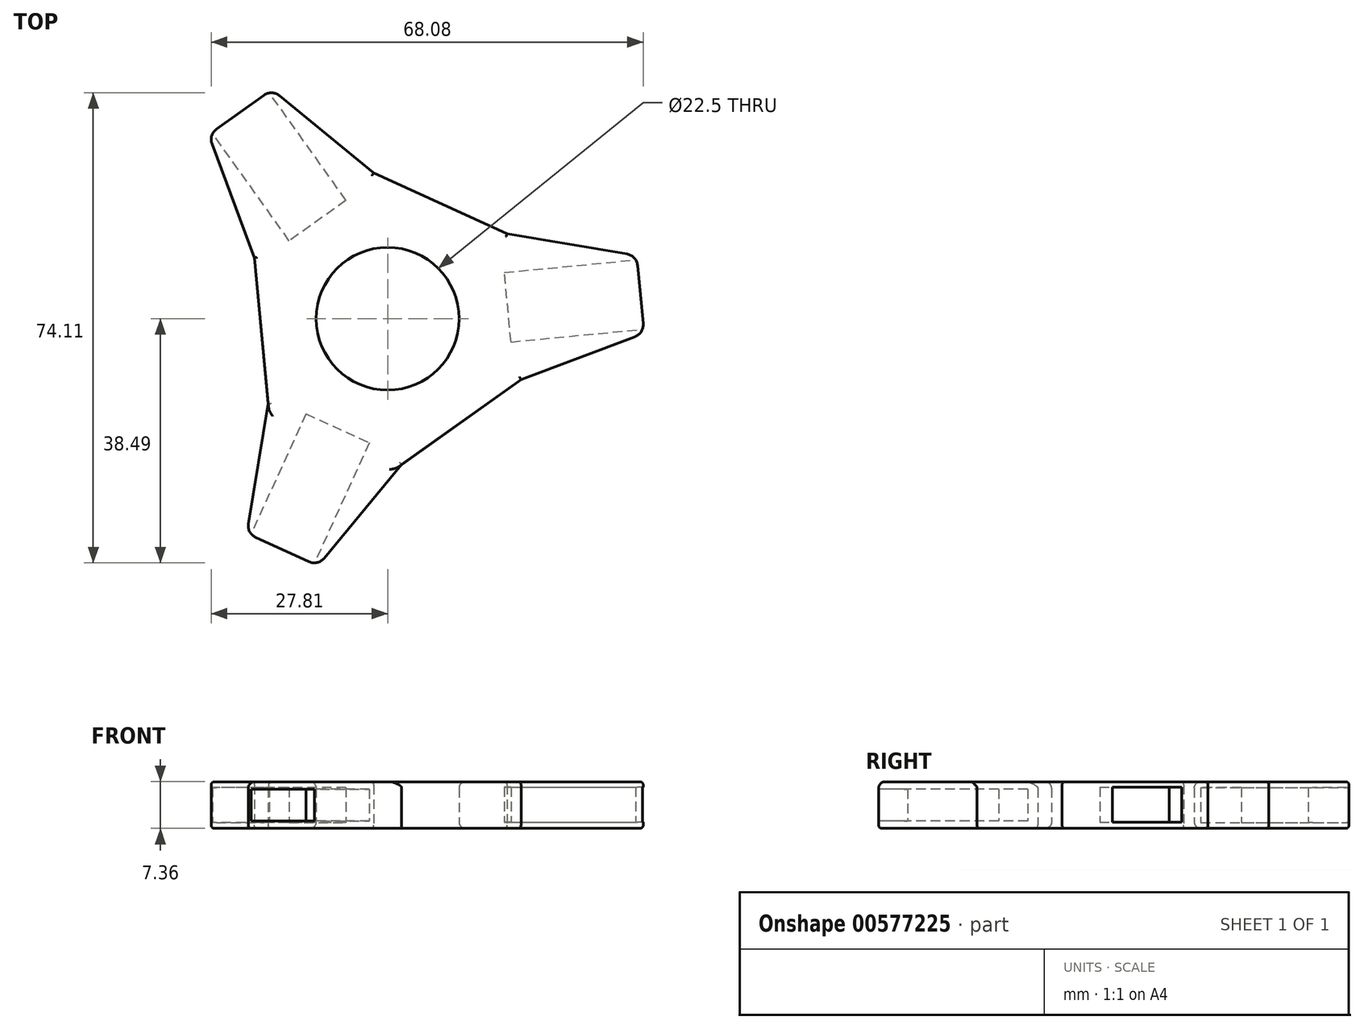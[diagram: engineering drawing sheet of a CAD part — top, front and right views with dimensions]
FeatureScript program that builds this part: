
annotation { "Feature Type Name" : "Feature", "Feature Type Description" : "" }
export const myFeature = defineFeature(function(context is Context, id is Id, definition is map)
    precondition{}
    {
        {
            var Q0;
            Q0=qCreatedBy(makeId("Top.planeOp"),FACE);
            var sketch = newSketch(context, id + "F0", { "sketchPlane" : qUnion([Q0])});
            skCircle(sketch, "E0", {"center": v(0, 0) * mm, "radius": 11.25 * mm});
            skPoint(sketch, "E1.0.midPoint", {"position": v(19.9, 1.91) * mm});
            skLineSegment(sketch, "E2", {"start": v(-21.01, 9.58) * mm, "end": v(-28.22, 29) * mm});
            skLineSegment(sketch, "E3", {"start": v(-28.22, 29) * mm, "end": v(-18.22, 36.13) * mm});
            skLineSegment(sketch, "E4", {"start": v(-18.22, 36.13) * mm, "end": v(-2.2, 22.99) * mm});
            skPoint(sketch, "E5.center", {"position": v(0, 0.71) * mm});
            skLineSegment(sketch, "E6.1.0", {"start": v(2.2, -22.99) * mm, "end": v(-11, -38.94) * mm});
            skLineSegment(sketch, "E6.1.4", {"start": v(-22.18, -33.85) * mm, "end": v(-18.8, -13.4) * mm});
            skLineSegment(sketch, "E6.1.5", {"start": v(-11, -38.94) * mm, "end": v(-22.18, -33.85) * mm});
            skLineSegment(sketch, "E6.2.0", {"start": v(18.8, 13.4) * mm, "end": v(39.23, 9.94) * mm});
            skLineSegment(sketch, "E6.2.4", {"start": v(40.4, -2.29) * mm, "end": v(21.01, -9.58) * mm});
            skLineSegment(sketch, "E6.2.5", {"start": v(39.23, 9.94) * mm, "end": v(40.4, -2.29) * mm});
            skCircle(sketch, "E7.cCircle", {"center": v(0, 0) * mm, "radius": 20 * mm, "construction": true});
            skLineSegment(sketch, "E7.0", {"start": v(18.8, 13.4) * mm, "end": v(21.01, -9.58) * mm});
            skLineSegment(sketch, "E7.2", {"start": v(2.2, -22.99) * mm, "end": v(-18.8, -13.4) * mm});
            skLineSegment(sketch, "E7.3", {"start": v(-18.8, -13.4) * mm, "end": v(-21.01, 9.58) * mm});
            skLineSegment(sketch, "E7.4", {"start": v(-21.01, 9.58) * mm, "end": v(-2.2, 22.99) * mm});
            skLineSegment(sketch, "E7.5", {"start": v(-2.2, 22.99) * mm, "end": v(18.8, 13.4) * mm});
            skLineSegment(sketch, "E8", {"start": v(2.2, -22.99) * mm, "end": v(21.01, -9.58) * mm});
            skSolve(sketch);
        }
        {
            var Q0;
            Q0 = qSketchRegion(id + "F0", true);
            extrude(context, id + "F1", {"entities" : qUnion([Q0]), "endBound" : BoundingType.SYMMETRIC, "depth" : 4.35 * mm, "offsetDistance" : 25 * mm});
        }
        {
            var Q0;
            Q0=makeQuery(id+"F1.opExtrude","CAP_FACE",FACE,{"disambiguationData":[OSD([sQuery(id+"F0.wireOp",EDGE,"E0"),sQuery(id+"F0.wireOp",EDGE,"E1.1"),sQuery(id+"F0.wireOp",EDGE,"E1.3"),sQuery(id+"F0.wireOp",EDGE,"E1.5"),sQuery(id+"F0.wireOp",EDGE,"E2"),sQuery(id+"F0.wireOp",EDGE,"E3"),sQuery(id+"F0.wireOp",EDGE,"E4"),sQuery(id+"F0.wireOp",EDGE,"IyGyZZ2j-7i47-TdS6-ERBN-ua2aBuEQpkr1.bottom"),sQuery(id+"F0.wireOp",EDGE,"IyGyZZ2j-7i47-TdS6-ERBN-ua2aBuEQpkr1.top"),sQuery(id+"F0.wireOp",EDGE,"IyGyZZ2j-7i47-TdS6-ERBN-ua2aBuEQpkr1.left"),sQuery(id+"F0.wireOp",EDGE,"IyGyZZ2j-7i47-TdS6-ERBN-ua2aBuEQpkr1.right"),sQuery(id+"F0.wireOp",EDGE,"MXUuy9MU-6Gwn-W3UW-Jdoq-sXBRnCOHbCZX.bottom"),sQuery(id+"F0.wireOp",EDGE,"MXUuy9MU-6Gwn-W3UW-Jdoq-sXBRnCOHbCZX.top"),sQuery(id+"F0.wireOp",EDGE,"MXUuy9MU-6Gwn-W3UW-Jdoq-sXBRnCOHbCZX.left"),sQuery(id+"F0.wireOp",EDGE,"MXUuy9MU-6Gwn-W3UW-Jdoq-sXBRnCOHbCZX.right"),sQuery(id+"F0.wireOp",EDGE,"6431977e-7dac-4d3b-9058-e1544c9c4d50.1.0"),sQuery(id+"F0.wireOp",EDGE,"6431977e-7dac-4d3b-9058-e1544c9c4d50.1.1"),sQuery(id+"F0.wireOp",EDGE,"6431977e-7dac-4d3b-9058-e1544c9c4d50.1.2"),sQuery(id+"F0.wireOp",EDGE,"6431977e-7dac-4d3b-9058-e1544c9c4d50.1.3"),sQuery(id+"F0.wireOp",EDGE,"6431977e-7dac-4d3b-9058-e1544c9c4d50.1.4"),sQuery(id+"F0.wireOp",EDGE,"6431977e-7dac-4d3b-9058-e1544c9c4d50.1.5"),sQuery(id+"F0.wireOp",EDGE,"6431977e-7dac-4d3b-9058-e1544c9c4d50.1.6"),sQuery(id+"F0.wireOp",EDGE,"6431977e-7dac-4d3b-9058-e1544c9c4d50.1.7"),sQuery(id+"F0.wireOp",EDGE,"6431977e-7dac-4d3b-9058-e1544c9c4d50.1.8"),sQuery(id+"F0.wireOp",EDGE,"6431977e-7dac-4d3b-9058-e1544c9c4d50.1.9"),sQuery(id+"F0.wireOp",EDGE,"6431977e-7dac-4d3b-9058-e1544c9c4d50.1.10"),sQuery(id+"F0.wireOp",EDGE,"6431977e-7dac-4d3b-9058-e1544c9c4d50.2.0"),sQuery(id+"F0.wireOp",EDGE,"6431977e-7dac-4d3b-9058-e1544c9c4d50.2.1"),sQuery(id+"F0.wireOp",EDGE,"6431977e-7dac-4d3b-9058-e1544c9c4d50.2.2"),sQuery(id+"F0.wireOp",EDGE,"6431977e-7dac-4d3b-9058-e1544c9c4d50.2.3"),sQuery(id+"F0.wireOp",EDGE,"6431977e-7dac-4d3b-9058-e1544c9c4d50.2.4"),sQuery(id+"F0.wireOp",EDGE,"6431977e-7dac-4d3b-9058-e1544c9c4d50.2.5"),sQuery(id+"F0.wireOp",EDGE,"6431977e-7dac-4d3b-9058-e1544c9c4d50.2.6"),sQuery(id+"F0.wireOp",EDGE,"6431977e-7dac-4d3b-9058-e1544c9c4d50.2.7"),sQuery(id+"F0.wireOp",EDGE,"6431977e-7dac-4d3b-9058-e1544c9c4d50.2.8"),sQuery(id+"F0.wireOp",EDGE,"6431977e-7dac-4d3b-9058-e1544c9c4d50.2.9"),sQuery(id+"F0.wireOp",EDGE,"6431977e-7dac-4d3b-9058-e1544c9c4d50.2.10")])],"isStart":false});
            var sketch = newSketch(context, id + "F2", { "sketchPlane" : qUnion([Q0])});
            skLineSegment(sketch, "E9", {"start": v(-22.18, -33.85) * mm, "end": v(-18.8, -13.4) * mm});
            skLineSegment(sketch, "E10", {"start": v(-28.22, 29) * mm, "end": v(-28.22, 29) * mm});
            skLineSegment(sketch, "E11", {"start": v(-28.22, 29) * mm, "end": v(-18.22, 36.13) * mm});
            skLineSegment(sketch, "E12", {"start": v(-18.22, 36.13) * mm, "end": v(-18.22, 36.13) * mm});
            skLineSegment(sketch, "E13", {"start": v(39.23, 9.94) * mm, "end": v(40.4, -2.29) * mm});
            skLineSegment(sketch, "E14", {"start": v(-11, -38.94) * mm, "end": v(-22.18, -33.85) * mm});
            skCircle(sketch, "E15", {"center": v(0, 0) * mm, "radius": 11.25 * mm});
            skLineSegment(sketch, "E16", {"start": v(39.23, 9.94) * mm, "end": v(39.23, 9.94) * mm});
            skLineSegment(sketch, "E17", {"start": v(40.4, -2.29) * mm, "end": v(40.4, -2.29) * mm});
            skLineSegment(sketch, "E18", {"start": v(-11, -38.94) * mm, "end": v(-11, -38.94) * mm});
            skLineSegment(sketch, "E19", {"start": v(-18.8, -13.4) * mm, "end": v(-21.01, 9.58) * mm});
            skLineSegment(sketch, "E20", {"start": v(-21.01, 9.58) * mm, "end": v(-28.22, 29) * mm});
            skLineSegment(sketch, "E21", {"start": v(-18.22, 36.13) * mm, "end": v(-2.2, 22.99) * mm});
            skLineSegment(sketch, "E22", {"start": v(-2.2, 22.99) * mm, "end": v(18.8, 13.4) * mm});
            skLineSegment(sketch, "E23", {"start": v(18.8, 13.4) * mm, "end": v(39.23, 9.94) * mm});
            skLineSegment(sketch, "E24", {"start": v(40.4, -2.29) * mm, "end": v(21.01, -9.58) * mm});
            skLineSegment(sketch, "E25", {"start": v(21.01, -9.58) * mm, "end": v(2.2, -22.99) * mm});
            skLineSegment(sketch, "E26", {"start": v(2.2, -22.99) * mm, "end": v(-11, -38.94) * mm});
            skSolve(sketch);
        }
        {
            var Q0;
            Q0 = qSketchRegion(id + "F2", true);
            extrude(context, id + "F3", {"entities" : qUnion([Q0]), "operationType" : NewBodyOperationType.ADD, "depth" : 1.5 * mm, "offsetDistance" : 25 * mm});
        }
        {
            var Q0;
            Q0=makeQuery(id+"F1.opExtrude","SWEPT_BODY",BODY,{"disambiguationData":[OSD([sQuery(id+"F0.wireOp",EDGE,"E0"),sQuery(id+"F0.wireOp",EDGE,"E1.1"),sQuery(id+"F0.wireOp",EDGE,"E1.3"),sQuery(id+"F0.wireOp",EDGE,"E1.5"),sQuery(id+"F0.wireOp",EDGE,"E2"),sQuery(id+"F0.wireOp",EDGE,"E3"),sQuery(id+"F0.wireOp",EDGE,"E4"),sQuery(id+"F0.wireOp",EDGE,"EbaCOkDP-zAhZ-bmKm-Rwlq-MVlfTA77LE2a"),sQuery(id+"F0.wireOp",EDGE,"XpNV4llA-Ck6J-PTxp-DKK9-vu7mp3MRyvdA"),sQuery(id+"F0.wireOp",EDGE,"A7reB7LC-x8tl-05Yz-VyCx-lSxhYCwyqfyA"),sQuery(id+"F0.wireOp",EDGE,"CRzMPJHI-l73M-eAgr-tN1m-DsJvh2o7b73Q"),sQuery(id+"F0.wireOp",EDGE,"E6.1.0"),sQuery(id+"F0.wireOp",EDGE,"E6.1.1"),sQuery(id+"F0.wireOp",EDGE,"E6.1.2"),sQuery(id+"F0.wireOp",EDGE,"E6.1.3"),sQuery(id+"F0.wireOp",EDGE,"E6.1.4"),sQuery(id+"F0.wireOp",EDGE,"E6.1.5"),sQuery(id+"F0.wireOp",EDGE,"E6.1.6"),sQuery(id+"F0.wireOp",EDGE,"E6.2.0"),sQuery(id+"F0.wireOp",EDGE,"E6.2.1"),sQuery(id+"F0.wireOp",EDGE,"E6.2.2"),sQuery(id+"F0.wireOp",EDGE,"E6.2.3"),sQuery(id+"F0.wireOp",EDGE,"E6.2.4"),sQuery(id+"F0.wireOp",EDGE,"E6.2.5"),sQuery(id+"F0.wireOp",EDGE,"E6.2.6")])]});
            var Q1;
            Q1=qCreatedBy(makeId("Top.planeOp"),FACE);
            mirror(context, id + "F4", {"operationType" : NewBodyOperationType.ADD, "entities" : qUnion([Q0]), "mirrorPlane" : qUnion([Q1])});
        }
        {
            var Q0;
            {var subQ0=makeQuery(id+"F3.boolean.opBoolean","MERGE",FACE,{"derivedFrom":[makeQuery(id+"F1.opExtrude","SWEPT_FACE",FACE,{"disambiguationData":[OSD([sQuery(id+"F0.wireOp",EDGE,"E6.2.5")])]}),makeQuery(id+"F3.opExtrude","SWEPT_FACE",FACE,{"disambiguationData":[OSD([sQuery(id+"F2.wireOp",EDGE,"E13")])]})]});Q0=makeQuery(id+"F4.boolean.opBoolean","MERGE",FACE,{"derivedFrom":[subQ0,makeQuery(id+"F4.opPattern","COPY",FACE,{"derivedFrom":subQ0,"instanceName":"1"})]});}
            var sketch = newSketch(context, id + "F5", { "sketchPlane" : qUnion([Q0])});
            skLineSegment(sketch, "E27.bottom", {"start": v(-5.5, 2.82) * mm, "end": v(5.5, 2.82) * mm});
            skLineSegment(sketch, "E27.top", {"start": v(-5.5, -2.67) * mm, "end": v(5.5, -2.67) * mm});
            skLineSegment(sketch, "E27.left", {"start": v(-5.5, 2.82) * mm, "end": v(-5.5, -2.67) * mm});
            skLineSegment(sketch, "E27.right", {"start": v(5.5, 2.82) * mm, "end": v(5.5, -2.67) * mm});
            skSolve(sketch);
        }
        {
            var Q0;
            Q0 = qSketchRegion(id + "F5", true);
            extrude(context, id + "F6", {"entities" : qUnion([Q0]), "operationType" : NewBodyOperationType.REMOVE, "oppositeDirection" : true, "depth" : 21 * mm, "offsetDistance" : 25 * mm});
        }
        {
            var Q0;
            {var subQ0=makeQuery(id+"F3.boolean.opBoolean","MERGE",FACE,{"derivedFrom":[makeQuery(id+"F1.opExtrude","SWEPT_FACE",FACE,{"disambiguationData":[OSD([sQuery(id+"F0.wireOp",EDGE,"E3")])]}),makeQuery(id+"F3.opExtrude","SWEPT_FACE",FACE,{"disambiguationData":[OSD([sQuery(id+"F2.wireOp",EDGE,"E11")])]})]});Q0=makeQuery(id+"F4.boolean.opBoolean","MERGE",FACE,{"derivedFrom":[subQ0,makeQuery(id+"F4.opPattern","COPY",FACE,{"derivedFrom":subQ0,"instanceName":"1"})]});}
            var sketch = newSketch(context, id + "F7", { "sketchPlane" : qUnion([Q0])});
            skLineSegment(sketch, "E28.left", {"start": v(-5.5, 2.75) * mm, "end": v(-5.5, -2.75) * mm});
            skLineSegment(sketch, "E29", {"start": v(-5.5, 2.75) * mm, "end": v(5.5, 2.75) * mm});
            skLineSegment(sketch, "E30", {"start": v(5.5, 2.75) * mm, "end": v(5.5, -2.75) * mm});
            skLineSegment(sketch, "E31", {"start": v(5.5, -2.75) * mm, "end": v(-5.5, -2.75) * mm});
            skSolve(sketch);
        }
        {
            var Q0;
            Q0 = qSketchRegion(id + "F7", true);
            extrude(context, id + "F8", {"entities" : qUnion([Q0]), "operationType" : NewBodyOperationType.REMOVE, "oppositeDirection" : true, "depth" : 21 * mm, "offsetDistance" : 25 * mm});
        }
        {
            var Q0;
            {var subQ0=makeQuery(id+"F3.boolean.opBoolean","MERGE",FACE,{"derivedFrom":[makeQuery(id+"F1.opExtrude","SWEPT_FACE",FACE,{"disambiguationData":[OSD([sQuery(id+"F0.wireOp",EDGE,"E6.1.5")])]}),makeQuery(id+"F3.opExtrude","SWEPT_FACE",FACE,{"disambiguationData":[OSD([sQuery(id+"F2.wireOp",EDGE,"E14")])]})]});Q0=makeQuery(id+"F4.boolean.opBoolean","MERGE",FACE,{"derivedFrom":[subQ0,makeQuery(id+"F4.opPattern","COPY",FACE,{"derivedFrom":subQ0,"instanceName":"1"})]});}
            var sketch = newSketch(context, id + "F9", { "sketchPlane" : qUnion([Q0])});
            skLineSegment(sketch, "E32.bottom", {"start": v(-5.5, 2.5) * mm, "end": v(5.5, 2.5) * mm});
            skLineSegment(sketch, "E32.top", {"start": v(-5.5, -2.5) * mm, "end": v(5.5, -2.5) * mm});
            skLineSegment(sketch, "E32.left", {"start": v(-5.5, 2.5) * mm, "end": v(-5.5, -2.5) * mm});
            skLineSegment(sketch, "E32.right", {"start": v(5.5, 2.5) * mm, "end": v(5.5, -2.5) * mm});
            skSolve(sketch);
        }
        {
            var Q0;
            Q0 = qSketchRegion(id + "F9", true);
            extrude(context, id + "F10", {"entities" : qUnion([Q0]), "operationType" : NewBodyOperationType.REMOVE, "oppositeDirection" : true, "depth" : 21 * mm, "offsetDistance" : 25 * mm});
        }
        {
            var Q0;
            {var subQ0=makeQuery(id+"F3.boolean.opBoolean","MERGE",EDGE,{"derivedFrom":[makeQuery(id+"F1.opExtrude","SWEPT_EDGE",EDGE,{"disambiguationData":[OSD([sQuery(id+"F0.wireOp",EDGE,"E3"),sQuery(id+"F0.wireOp",EDGE,"E4")])]}),makeQuery(id+"F3.opExtrude","SWEPT_EDGE",EDGE,{"disambiguationData":[OSD([sQuery(id+"F2.wireOp",EDGE,"E11"),sQuery(id+"F2.wireOp",EDGE,"E21")])]})]});Q0=makeQuery(id+"F4.boolean.opBoolean","MERGE",EDGE,{"derivedFrom":[subQ0,makeQuery(id+"F4.opPattern","COPY",EDGE,{"derivedFrom":subQ0,"instanceName":"1"})]});}
            var Q1;
            {var subQ0=makeQuery(id+"F3.boolean.opBoolean","MERGE",EDGE,{"derivedFrom":[makeQuery(id+"F1.opExtrude","SWEPT_EDGE",EDGE,{"disambiguationData":[OSD([sQuery(id+"F0.wireOp",EDGE,"E2"),sQuery(id+"F0.wireOp",EDGE,"E3")])]}),makeQuery(id+"F3.opExtrude","SWEPT_EDGE",EDGE,{"disambiguationData":[OSD([sQuery(id+"F2.wireOp",EDGE,"E11"),sQuery(id+"F2.wireOp",EDGE,"E20")])]})]});Q1=makeQuery(id+"F4.boolean.opBoolean","MERGE",EDGE,{"derivedFrom":[subQ0,makeQuery(id+"F4.opPattern","COPY",EDGE,{"derivedFrom":subQ0,"instanceName":"1"})]});}
            var Q2;
            {var subQ0=makeQuery(id+"F3.boolean.opBoolean","MERGE",EDGE,{"derivedFrom":[makeQuery(id+"F1.opExtrude","SWEPT_EDGE",EDGE,{"disambiguationData":[OSD([sQuery(id+"F0.wireOp",EDGE,"E6.1.4"),sQuery(id+"F0.wireOp",EDGE,"E6.1.5")])]}),makeQuery(id+"F3.opExtrude","SWEPT_EDGE",EDGE,{"disambiguationData":[OSD([sQuery(id+"F2.wireOp",EDGE,"E9"),sQuery(id+"F2.wireOp",EDGE,"E14")])]})]});Q2=makeQuery(id+"F4.boolean.opBoolean","MERGE",EDGE,{"derivedFrom":[subQ0,makeQuery(id+"F4.opPattern","COPY",EDGE,{"derivedFrom":subQ0,"instanceName":"1"})]});}
            var Q3;
            {var subQ0=makeQuery(id+"F3.boolean.opBoolean","MERGE",EDGE,{"derivedFrom":[makeQuery(id+"F1.opExtrude","SWEPT_EDGE",EDGE,{"disambiguationData":[OSD([sQuery(id+"F0.wireOp",EDGE,"E6.1.0"),sQuery(id+"F0.wireOp",EDGE,"E6.1.5")])]}),makeQuery(id+"F3.opExtrude","SWEPT_EDGE",EDGE,{"disambiguationData":[OSD([sQuery(id+"F2.wireOp",EDGE,"E14"),sQuery(id+"F2.wireOp",EDGE,"E26")])]})]});Q3=makeQuery(id+"F4.boolean.opBoolean","MERGE",EDGE,{"derivedFrom":[subQ0,makeQuery(id+"F4.opPattern","COPY",EDGE,{"derivedFrom":subQ0,"instanceName":"1"})]});}
            var Q4;
            {var subQ0=makeQuery(id+"F3.boolean.opBoolean","MERGE",EDGE,{"derivedFrom":[makeQuery(id+"F1.opExtrude","SWEPT_EDGE",EDGE,{"disambiguationData":[OSD([sQuery(id+"F0.wireOp",EDGE,"E6.2.4"),sQuery(id+"F0.wireOp",EDGE,"E6.2.5")])]}),makeQuery(id+"F3.opExtrude","SWEPT_EDGE",EDGE,{"disambiguationData":[OSD([sQuery(id+"F2.wireOp",EDGE,"E13"),sQuery(id+"F2.wireOp",EDGE,"E24")])]})]});Q4=makeQuery(id+"F4.boolean.opBoolean","MERGE",EDGE,{"derivedFrom":[subQ0,makeQuery(id+"F4.opPattern","COPY",EDGE,{"derivedFrom":subQ0,"instanceName":"1"})]});}
            var Q5;
            {var subQ0=makeQuery(id+"F3.boolean.opBoolean","MERGE",EDGE,{"derivedFrom":[makeQuery(id+"F1.opExtrude","SWEPT_EDGE",EDGE,{"disambiguationData":[OSD([sQuery(id+"F0.wireOp",EDGE,"E6.2.0"),sQuery(id+"F0.wireOp",EDGE,"E6.2.5")])]}),makeQuery(id+"F3.opExtrude","SWEPT_EDGE",EDGE,{"disambiguationData":[OSD([sQuery(id+"F2.wireOp",EDGE,"E13"),sQuery(id+"F2.wireOp",EDGE,"E23")])]})]});Q5=makeQuery(id+"F4.boolean.opBoolean","MERGE",EDGE,{"derivedFrom":[subQ0,makeQuery(id+"F4.opPattern","COPY",EDGE,{"derivedFrom":subQ0,"instanceName":"1"})]});}
            fillet(context, id + "F11", {"entities" : qUnion([Q0, Q1, Q2, Q3, Q4, Q5]), "radius" : 2 * mm, "tangentPropagation" : true, "allowEdgeOverflow" : false});
        }
        {
            var Q0;
            Q0=makeQuery(id+"F3.opExtrude","CAP_EDGE",EDGE,{"disambiguationData":[OSD([sQuery(id+"F2.wireOp",EDGE,"E14")])],"isStart":false});
            fillet(context, id + "F12", {"entities" : qUnion([Q0]), "radius" : 1 * mm, "tangentPropagation" : true, "allowEdgeOverflow" : false});
        }
        {
            var Q0;
            Q0=makeQuery(id+"F3.opExtrude","CAP_EDGE",EDGE,{"disambiguationData":[OSD([sQuery(id+"F2.wireOp",EDGE,"E24")])],"isStart":false});
            fillet(context, id + "F13", {"entities" : qUnion([Q0]), "radius" : .5 * mm, "tangentPropagation" : true, "allowEdgeOverflow" : false});
        }
        {
            var Q0;
            Q0=makeQuery(id+"F3.opExtrude","CAP_EDGE",EDGE,{"disambiguationData":[OSD([sQuery(id+"F2.wireOp",EDGE,"E11")])],"isStart":false});
            fillet(context, id + "F14", {"entities" : qUnion([Q0]), "radius" : .5 * mm, "tangentPropagation" : true, "allowEdgeOverflow" : false});
        }
        {
            var Q0;
            Q0=makeQuery(id+"F3.opExtrude","CAP_EDGE",EDGE,{"disambiguationData":[OSD([sQuery(id+"F2.wireOp",EDGE,"E19")])],"isStart":false});
            var Q1;
            Q1=makeQuery(id+"F3.opExtrude","CAP_EDGE",EDGE,{"disambiguationData":[OSD([sQuery(id+"F2.wireOp",EDGE,"E25")])],"isStart":false});
            var Q2;
            Q2=makeQuery(id+"F3.opExtrude","CAP_EDGE",EDGE,{"disambiguationData":[OSD([sQuery(id+"F2.wireOp",EDGE,"E22")])],"isStart":false});
            fillet(context, id + "F15", {"entities" : qUnion([Q0, Q1, Q2]), "radius" : .5 * mm, "tangentPropagation" : true, "allowEdgeOverflow" : false});
        }
        {
            var Q0;
            Q0=makeQuery(id+"F4.opPattern","COPY",EDGE,{"derivedFrom":makeQuery(id+"F3.opExtrude","CAP_EDGE",EDGE,{"disambiguationData":[OSD([sQuery(id+"F2.wireOp",EDGE,"E20")])],"isStart":false}),"instanceName":"1"});
            fillet(context, id + "F16", {"entities" : qUnion([Q0]), "radius" : .5 * mm, "tangentPropagation" : true, "allowEdgeOverflow" : false});
        }
        {
            var Q0;
            Q0=makeQuery(id+"F4.opPattern","COPY",EDGE,{"derivedFrom":makeQuery(id+"F3.opExtrude","CAP_EDGE",EDGE,{"disambiguationData":[OSD([sQuery(id+"F2.wireOp",EDGE,"E23")])],"isStart":false}),"instanceName":"1"});
            fillet(context, id + "F17", {"entities" : qUnion([Q0]), "radius" : .5 * mm, "tangentPropagation" : true, "allowEdgeOverflow" : false});
        }
        {
            var Q0;
            Q0=makeQuery(id+"F4.opPattern","COPY",EDGE,{"derivedFrom":makeQuery(id+"F3.opExtrude","CAP_EDGE",EDGE,{"disambiguationData":[OSD([sQuery(id+"F2.wireOp",EDGE,"E26")])],"isStart":false}),"instanceName":"1"});
            fillet(context, id + "F18", {"entities" : qUnion([Q0]), "radius" : .5 * mm, "tangentPropagation" : true, "allowEdgeOverflow" : false});
        }
        {
            var Q0;
            Q0=makeQuery(id+"F4.opPattern","COPY",EDGE,{"derivedFrom":makeQuery(id+"F3.opExtrude","CAP_EDGE",EDGE,{"disambiguationData":[OSD([sQuery(id+"F2.wireOp",EDGE,"E19")])],"isStart":false}),"instanceName":"1"});
            var Q1;
            Q1=makeQuery(id+"F4.opPattern","COPY",EDGE,{"derivedFrom":makeQuery(id+"F3.opExtrude","CAP_EDGE",EDGE,{"disambiguationData":[OSD([sQuery(id+"F2.wireOp",EDGE,"E25")])],"isStart":false}),"instanceName":"1"});
            var Q2;
            Q2=makeQuery(id+"F4.opPattern","COPY",EDGE,{"derivedFrom":makeQuery(id+"F3.opExtrude","CAP_EDGE",EDGE,{"disambiguationData":[OSD([sQuery(id+"F2.wireOp",EDGE,"E22")])],"isStart":false}),"instanceName":"1"});
            fillet(context, id + "F19", {"entities" : qUnion([Q0, Q1, Q2]), "radius" : .5 * mm, "tangentPropagation" : true, "allowEdgeOverflow" : false});
        }
        {
            var Q0;
            Q0=makeQuery(id+"F3.opExtrude","CAP_EDGE",EDGE,{"disambiguationData":[OSD([sQuery(id+"F2.wireOp",EDGE,"E15")])],"isStart":false});
            var Q1;
            Q1=makeQuery(id+"F4.opPattern","COPY",EDGE,{"derivedFrom":makeQuery(id+"F3.opExtrude","CAP_EDGE",EDGE,{"disambiguationData":[OSD([sQuery(id+"F2.wireOp",EDGE,"E15")])],"isStart":false}),"instanceName":"1"});
            fillet(context, id + "F20", {"entities" : qUnion([Q0, Q1]), "radius" : 1 * mm, "tangentPropagation" : true, "allowEdgeOverflow" : false});
        }
    });
